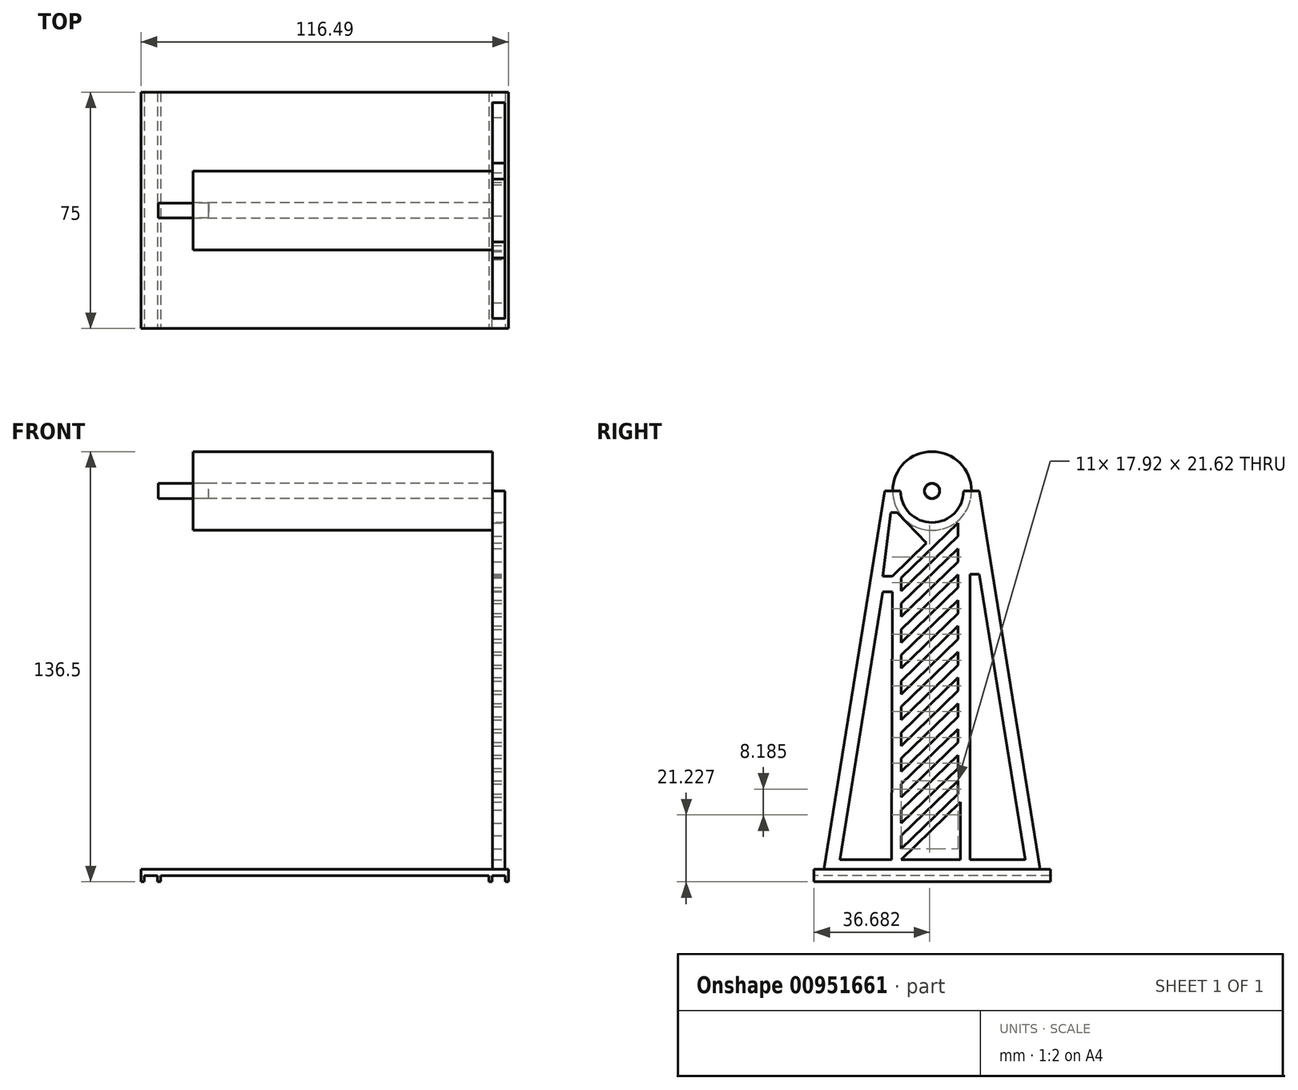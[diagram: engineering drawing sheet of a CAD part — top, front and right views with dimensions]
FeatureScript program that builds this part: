
annotation { "Feature Type Name" : "Feature", "Feature Type Description" : "" }
export const myFeature = defineFeature(function(context is Context, id is Id, definition is map)
    precondition{}
    {
        {
            var Q0;
            Q0=qCreatedBy(makeId("Right.planeOp"),FACE);
            var sketch = newSketch(context, id + "F0", { "sketchPlane" : qUnion([Q0])});
            skCircle(sketch, "E0", {"center": v(0, 0) * mm, "radius": 2.38 * mm});
            skSolve(sketch);
        }
        {
            var Q0;
            Q0=makeQuery(id+"F0.imprint","IMPRINT",FACE,{"disambiguationData":[TD([[makeQuery(id+"F0.imprint","IMPRINT",EDGE,{"derivedFrom":sQuery(id+"F0.wireOp",EDGE,"E0")}),1.0]])]});
            extrude(context, id + "F1", {"entities" : qUnion([Q0]), "depth" : 16 * mm, "offsetDistance" : 25 * mm});
        }
        {
            var Q0;
            Q0=makeQuery(id+"F1.opExtrude","CAP_FACE",FACE,{"disambiguationData":[OSD([sQuery(id+"F0.wireOp",EDGE,"E0")])],"isStart":false});
            var sketch = newSketch(context, id + "F2", { "sketchPlane" : qUnion([Q0])});
            skCircle(sketch, "E1.0.0", {"center": v(0, 0) * mm, "radius": 2.38 * mm});
            skCircle(sketch, "E2", {"center": v(0, 0) * mm, "radius": 12.5 * mm});
            skCircle(sketch, "E3", {"center": v(0, 0) * mm, "radius": 2.45 * mm});
            skSolve(sketch);
        }
        {
            var Q0;
            Q0 = qSketchRegion(id + "F2", true);
            extrude(context, id + "F3", {"entities" : qUnion([Q0]), "depth" : 90 * mm, "offsetDistance" : 25 * mm, "hasSecondDirection" : true, "secondDirectionOppositeDirection" : true, "secondDirectionDepth" : 5 * mm});
        }
        {
            var Q0;
            Q0=makeQuery(id+"F3.opExtrude","CAP_FACE",FACE,{"disambiguationData":[OSD([sQuery(id+"F2.wireOp",EDGE,"E2")])],"isStart":false});
            var sketch = newSketch(context, id + "F4", { "sketchPlane" : qUnion([Q0])});
            skCircle(sketch, "E4", {"center": v(0, 0) * mm, "radius": 10 * mm});
            skCircle(sketch, "E5", {"center": v(0, 0) * mm, "radius": 15 * mm});
            skLineSegment(sketch, "E6", {"start": v(0, 0) * mm, "end": v(15, 0) * mm});
            skLineSegment(sketch, "E7", {"start": v(0, 0) * mm, "end": v(-15, 0) * mm});
            skSolve(sketch);
        }
        {
            var Q0;
            {var subQ0=sQuery(id+"F4.wireOp",EDGE,"E6");var subQ1=sQuery(id+"F4.wireOp",EDGE,"E5");var subQ2=makeQuery(id+"F4.imprint","INTERSECT",VERTEX,{"derivedFrom":[subQ1,subQ0]});Q0=makeQuery(id+"F4.imprint","IMPRINT",FACE,{"disambiguationData":[TD([[makeQuery(id+"F4.imprint","IMPRINT",EDGE,{"disambiguationData":[TD([[subQ2,1.0]])],"derivedFrom":subQ1}),1.0]])]});}
            var Q1;
            {var subQ0=sQuery(id+"F4.wireOp",EDGE,"E6");var subQ1=sQuery(id+"F4.wireOp",EDGE,"E4");var subQ2=makeQuery(id+"F4.imprint","INTERSECT",VERTEX,{"derivedFrom":[subQ1,subQ0]});Q1=makeQuery(id+"F4.imprint","IMPRINT",FACE,{"disambiguationData":[TD([[makeQuery(id+"F4.imprint","IMPRINT",EDGE,{"disambiguationData":[TD([[subQ2,1.0]])],"derivedFrom":subQ1}),-1.0]])]});}
            extrude(context, id + "F5", {"entities" : qUnion([Q0, Q1]), "depth" : 4 * mm, "offsetDistance" : 25 * mm});
        }
        {
            var Q0;
            Q0=makeQuery(id+"F5.opExtrude","CAP_FACE",FACE,{"disambiguationData":[OSD([sQuery(id+"F4.wireOp",EDGE,"E4"),sQuery(id+"F4.wireOp",EDGE,"E5"),sQuery(id+"F4.wireOp",EDGE,"E6"),sQuery(id+"F4.wireOp",EDGE,"E7")])],"isStart":false});
            var sketch = newSketch(context, id + "F6", { "sketchPlane" : qUnion([Q0])});
            skArc(sketch, "E8.0.0", {"start": v(10, 0) * mm, "mid": v(0, -10) * mm, "end": v(-10, 0) * mm});
            skLineSegment(sketch, "E8.0.1", {"start": v(-10, 0) * mm, "end": v(-15, 0) * mm});
            skArc(sketch, "E8.0.2", {"start": v(-15, 0) * mm, "mid": v(0, -15) * mm, "end": v(15, 0) * mm});
            skLineSegment(sketch, "E8.0.3", {"start": v(15, 0) * mm, "end": v(10, 0) * mm});
            skLineSegment(sketch, "E9", {"start": v(-15, 0) * mm, "end": v(-34.26, -120) * mm});
            skLineSegment(sketch, "E10", {"start": v(15, 0) * mm, "end": v(34.26, -120) * mm});
            skLineSegment(sketch, "E11", {"start": v(34.26, -120) * mm, "end": v(-34.26, -120) * mm});
            skCircle(sketch, "E12.0.0", {"center": v(0, 0) * mm, "radius": 12.5 * mm});
            skLineSegment(sketch, "E13", {"start": v(0, 12.5) * mm, "end": v(18.93, 12.5) * mm});
            skSolve(sketch);
        }
        {
            var Q0;
            Q0=makeQuery(id+"F6.imprint","IMPRINT",FACE,{"disambiguationData":[TD([[makeQuery(id+"F6.imprint","IMPRINT",EDGE,{"derivedFrom":sQuery(id+"F6.wireOp",EDGE,"E8.0.2")}),-1.0]])]});
            var Q1;
            {var subQ0=sQuery(id+"F6.wireOp",EDGE,"E8.0.2");Q1=makeQuery(id+"F6.imprint","IMPRINT",FACE,{"disambiguationData":[TD([[makeQuery(id+"F6.imprint","IMPRINT",EDGE,{"derivedFrom":subQ0}),1.0]])]});}
            var Q2;
            {var subQ0=sQuery(id+"F6.wireOp",EDGE,"E8.0.0");Q2=makeQuery(id+"F6.imprint","IMPRINT",FACE,{"disambiguationData":[TD([[makeQuery(id+"F6.imprint","IMPRINT",EDGE,{"derivedFrom":subQ0}),-1.0]])]});}
            extrude(context, id + "F7", {"entities" : qUnion([Q0, Q1, Q2]), "operationType" : NewBodyOperationType.ADD, "oppositeDirection" : true, "depth" : 4 * mm, "offsetDistance" : 25 * mm});
        }
        {
            var Q0;
            Q0=makeQuery(id+"F7.boolean.opBoolean","MERGE",FACE,{"derivedFrom":[makeQuery(id+"F5.opExtrude","CAP_FACE",FACE,{"disambiguationData":[OSD([sQuery(id+"F4.wireOp",EDGE,"E4"),sQuery(id+"F4.wireOp",EDGE,"E5"),sQuery(id+"F4.wireOp",EDGE,"E6"),sQuery(id+"F4.wireOp",EDGE,"E7")])],"isStart":false}),makeQuery(id+"F7.opExtrude","CAP_FACE",FACE,{"disambiguationData":[OSD([sQuery(id+"F6.wireOp",EDGE,"E8.0.0"),sQuery(id+"F6.wireOp",EDGE,"E8.0.1"),sQuery(id+"F6.wireOp",EDGE,"E8.0.3"),sQuery(id+"F6.wireOp",EDGE,"E9"),sQuery(id+"F6.wireOp",EDGE,"E10"),sQuery(id+"F6.wireOp",EDGE,"E11")])],"isStart":true})]});
            var sketch = newSketch(context, id + "F8", { "sketchPlane" : qUnion([Q0])});
            skLineSegment(sketch, "E14", {"start": v(-9.74, -27.54) * mm, "end": v(8.18, -10.11) * mm});
            skLineSegment(sketch, "E15", {"start": v(8.18, -10.11) * mm, "end": v(8.18, -14.3) * mm});
            skLineSegment(sketch, "E16", {"start": v(8.18, -14.3) * mm, "end": v(-9.74, -31.73) * mm});
            skLineSegment(sketch, "E17", {"start": v(-9.74, -31.73) * mm, "end": v(-9.74, -27.54) * mm});
            skLineSegment(sketch, "E18", {"start": v(-9.74, -35.73) * mm, "end": v(8.18, -18.3) * mm});
            skLineSegment(sketch, "E19", {"start": v(8.18, -18.3) * mm, "end": v(8.18, -22.48) * mm});
            skLineSegment(sketch, "E20", {"start": v(8.18, -22.48) * mm, "end": v(-9.74, -39.91) * mm});
            skLineSegment(sketch, "E21", {"start": v(-9.74, -39.91) * mm, "end": v(-9.74, -35.73) * mm});
            skLineSegment(sketch, "E22", {"start": v(-9.74, -43.91) * mm, "end": v(8.18, -26.48) * mm});
            skLineSegment(sketch, "E23", {"start": v(8.18, -26.48) * mm, "end": v(8.18, -30.67) * mm});
            skLineSegment(sketch, "E24", {"start": v(8.18, -30.67) * mm, "end": v(-9.74, -48.1) * mm});
            skLineSegment(sketch, "E25", {"start": v(-9.74, -48.1) * mm, "end": v(-9.74, -43.91) * mm});
            skLineSegment(sketch, "E26", {"start": v(-9.74, -52.1) * mm, "end": v(8.18, -34.67) * mm});
            skLineSegment(sketch, "E27", {"start": v(8.18, -34.67) * mm, "end": v(8.18, -38.85) * mm});
            skLineSegment(sketch, "E28", {"start": v(8.18, -38.85) * mm, "end": v(-9.74, -56.28) * mm});
            skLineSegment(sketch, "E29", {"start": v(-9.74, -56.28) * mm, "end": v(-9.74, -52.1) * mm});
            skLineSegment(sketch, "E30", {"start": v(-9.74, -60.28) * mm, "end": v(8.18, -42.85) * mm});
            skLineSegment(sketch, "E31", {"start": v(8.18, -42.85) * mm, "end": v(8.18, -47.04) * mm});
            skLineSegment(sketch, "E32", {"start": v(8.18, -47.04) * mm, "end": v(-9.74, -64.47) * mm});
            skLineSegment(sketch, "E33", {"start": v(-9.74, -64.47) * mm, "end": v(-9.74, -60.28) * mm});
            skLineSegment(sketch, "E34", {"start": v(-9.74, -68.47) * mm, "end": v(8.18, -51.04) * mm});
            skLineSegment(sketch, "E35", {"start": v(8.18, -51.04) * mm, "end": v(8.18, -55.22) * mm});
            skLineSegment(sketch, "E36", {"start": v(8.18, -55.22) * mm, "end": v(-9.74, -72.66) * mm});
            skLineSegment(sketch, "E37", {"start": v(-9.74, -72.66) * mm, "end": v(-9.74, -68.47) * mm});
            skLineSegment(sketch, "E38", {"start": v(-9.74, -76.66) * mm, "end": v(8.18, -59.22) * mm});
            skLineSegment(sketch, "E39", {"start": v(8.18, -59.22) * mm, "end": v(8.18, -63.4) * mm});
            skLineSegment(sketch, "E40", {"start": v(8.18, -63.4) * mm, "end": v(-9.74, -80.84) * mm});
            skLineSegment(sketch, "E41", {"start": v(-9.74, -80.84) * mm, "end": v(-9.74, -76.66) * mm});
            skLineSegment(sketch, "E42", {"start": v(-9.74, -84.84) * mm, "end": v(8.18, -67.4) * mm});
            skLineSegment(sketch, "E43", {"start": v(8.18, -67.4) * mm, "end": v(8.18, -71.6) * mm});
            skLineSegment(sketch, "E44", {"start": v(8.18, -71.6) * mm, "end": v(-9.74, -89.03) * mm});
            skLineSegment(sketch, "E45", {"start": v(-9.74, -89.03) * mm, "end": v(-9.74, -84.84) * mm});
            skLineSegment(sketch, "E46", {"start": v(-9.74, -93.03) * mm, "end": v(8.18, -75.6) * mm});
            skLineSegment(sketch, "E47", {"start": v(8.18, -75.6) * mm, "end": v(8.18, -79.78) * mm});
            skLineSegment(sketch, "E48", {"start": v(8.18, -79.78) * mm, "end": v(-9.74, -97.21) * mm});
            skLineSegment(sketch, "E49", {"start": v(-9.74, -97.21) * mm, "end": v(-9.74, -93.03) * mm});
            skLineSegment(sketch, "E50", {"start": v(-9.74, -101.21) * mm, "end": v(8.18, -83.78) * mm});
            skLineSegment(sketch, "E51", {"start": v(8.18, -83.78) * mm, "end": v(8.18, -87.96) * mm});
            skLineSegment(sketch, "E52", {"start": v(8.18, -87.96) * mm, "end": v(-9.74, -105.4) * mm});
            skLineSegment(sketch, "E53", {"start": v(-9.74, -105.4) * mm, "end": v(-9.74, -101.21) * mm});
            skLineSegment(sketch, "E54", {"start": v(-9.74, -109.4) * mm, "end": v(8.18, -91.96) * mm});
            skLineSegment(sketch, "E55", {"start": v(8.18, -91.96) * mm, "end": v(8.18, -96.15) * mm});
            skLineSegment(sketch, "E56", {"start": v(8.18, -96.15) * mm, "end": v(-9.74, -113.58) * mm});
            skLineSegment(sketch, "E57", {"start": v(-9.74, -113.58) * mm, "end": v(-9.74, -109.4) * mm});
            skLineSegment(sketch, "E58", {"start": v(-9.74, -116.96) * mm, "end": v(9, -98.73) * mm});
            skLineSegment(sketch, "E59", {"start": v(9, -98.73) * mm, "end": v(12, -98.73) * mm});
            skLineSegment(sketch, "E60", {"start": v(12, -98.73) * mm, "end": v(12, -26.38) * mm});
            skLineSegment(sketch, "E61", {"start": v(12, -26.38) * mm, "end": v(15, -26.38) * mm});
            skLineSegment(sketch, "E62", {"start": v(15, -26.38) * mm, "end": v(29.54, -116.96) * mm});
            skLineSegment(sketch, "E63", {"start": v(29.54, -116.96) * mm, "end": v(-9.74, -116.96) * mm});
            skLineSegment(sketch, "E64", {"start": v(-12.83, -116.96) * mm, "end": v(-29.24, -116.96) * mm});
            skLineSegment(sketch, "E65", {"start": v(-29.24, -116.96) * mm, "end": v(-15.6, -31.99) * mm});
            skLineSegment(sketch, "E66", {"start": v(-15.6, -31.99) * mm, "end": v(-12.6, -31.99) * mm});
            skLineSegment(sketch, "E67", {"start": v(-12.6, -31.99) * mm, "end": v(-12.83, -116.96) * mm});
            skLineSegment(sketch, "E68", {"start": v(-15.6, -27.04) * mm, "end": v(-12.6, -27.04) * mm});
            skLineSegment(sketch, "E69", {"start": v(-12.6, -27.04) * mm, "end": v(-1.72, -16.46) * mm});
            skLineSegment(sketch, "E70", {"start": v(-1.72, -16.46) * mm, "end": v(-11.07, -6.84) * mm});
            skLineSegment(sketch, "E71", {"start": v(-11.07, -6.84) * mm, "end": v(-13.07, -6.84) * mm});
            skLineSegment(sketch, "E72", {"start": v(-13.07, -6.84) * mm, "end": v(-15.6, -27.04) * mm});
            skLineSegment(sketch, "E73", {"start": v(9, -98.73) * mm, "end": v(9, -116.96) * mm});
            skLineSegment(sketch, "E74", {"start": v(12, -98.73) * mm, "end": v(12, -116.96) * mm});
            skSolve(sketch);
        }
        {
            var Q0;
            Q0=makeQuery(id+"F8.imprint","IMPRINT",FACE,{"disambiguationData":[TD([[makeQuery(id+"F8.imprint","IMPRINT",EDGE,{"derivedFrom":sQuery(id+"F8.wireOp",EDGE,"E14")}),-1.0]])]});
            var Q1;
            Q1=makeQuery(id+"F8.imprint","IMPRINT",FACE,{"disambiguationData":[TD([[makeQuery(id+"F8.imprint","IMPRINT",EDGE,{"derivedFrom":sQuery(id+"F8.wireOp",EDGE,"E18")}),-1.0]])]});
            var Q2;
            Q2=makeQuery(id+"F8.imprint","IMPRINT",FACE,{"disambiguationData":[TD([[makeQuery(id+"F8.imprint","IMPRINT",EDGE,{"derivedFrom":sQuery(id+"F8.wireOp",EDGE,"E22")}),-1.0]])]});
            var Q3;
            Q3=makeQuery(id+"F8.imprint","IMPRINT",FACE,{"disambiguationData":[TD([[makeQuery(id+"F8.imprint","IMPRINT",EDGE,{"derivedFrom":sQuery(id+"F8.wireOp",EDGE,"E26")}),-1.0]])]});
            var Q4;
            Q4=makeQuery(id+"F8.imprint","IMPRINT",FACE,{"disambiguationData":[TD([[makeQuery(id+"F8.imprint","IMPRINT",EDGE,{"derivedFrom":sQuery(id+"F8.wireOp",EDGE,"E30")}),-1.0]])]});
            var Q5;
            Q5=makeQuery(id+"F8.imprint","IMPRINT",FACE,{"disambiguationData":[TD([[makeQuery(id+"F8.imprint","IMPRINT",EDGE,{"derivedFrom":sQuery(id+"F8.wireOp",EDGE,"E34")}),-1.0]])]});
            var Q6;
            Q6=makeQuery(id+"F8.imprint","IMPRINT",FACE,{"disambiguationData":[TD([[makeQuery(id+"F8.imprint","IMPRINT",EDGE,{"derivedFrom":sQuery(id+"F8.wireOp",EDGE,"E38")}),-1.0]])]});
            var Q7;
            Q7=makeQuery(id+"F8.imprint","IMPRINT",FACE,{"disambiguationData":[TD([[makeQuery(id+"F8.imprint","IMPRINT",EDGE,{"derivedFrom":sQuery(id+"F8.wireOp",EDGE,"E42")}),-1.0]])]});
            var Q8;
            Q8=makeQuery(id+"F8.imprint","IMPRINT",FACE,{"disambiguationData":[TD([[makeQuery(id+"F8.imprint","IMPRINT",EDGE,{"derivedFrom":sQuery(id+"F8.wireOp",EDGE,"E46")}),-1.0]])]});
            var Q9;
            Q9=makeQuery(id+"F8.imprint","IMPRINT",FACE,{"disambiguationData":[TD([[makeQuery(id+"F8.imprint","IMPRINT",EDGE,{"derivedFrom":sQuery(id+"F8.wireOp",EDGE,"E50")}),-1.0]])]});
            var Q10;
            Q10=makeQuery(id+"F8.imprint","IMPRINT",FACE,{"disambiguationData":[TD([[makeQuery(id+"F8.imprint","IMPRINT",EDGE,{"derivedFrom":sQuery(id+"F8.wireOp",EDGE,"E54")}),-1.0]])]});
            var Q11;
            Q11=makeQuery(id+"F8.imprint","IMPRINT",FACE,{"disambiguationData":[TD([[makeQuery(id+"F8.imprint","IMPRINT",EDGE,{"derivedFrom":sQuery(id+"F8.wireOp",EDGE,"E68")}),1.0]])]});
            var Q12;
            Q12=makeQuery(id+"F8.imprint","IMPRINT",FACE,{"disambiguationData":[TD([[makeQuery(id+"F8.imprint","IMPRINT",EDGE,{"derivedFrom":sQuery(id+"F8.wireOp",EDGE,"E64")}),-1.0]])]});
            var Q13;
            Q13=makeQuery(id+"F8.imprint","IMPRINT",FACE,{"disambiguationData":[TD([[makeQuery(id+"F8.imprint","IMPRINT",EDGE,{"derivedFrom":sQuery(id+"F8.wireOp",EDGE,"E60")}),-1.0]])]});
            var Q14;
            {var subQ0=sQuery(id+"F8.wireOp",EDGE,"E58");Q14=makeQuery(id+"F8.imprint","IMPRINT",FACE,{"disambiguationData":[TD([[makeQuery(id+"F8.imprint","IMPRINT",EDGE,{"derivedFrom":subQ0}),-1.0]])]});}
            extrude(context, id + "F9", {"entities" : qUnion([Q0, Q1, Q2, Q3, Q4, Q5, Q6, Q7, Q8, Q9, Q10, Q11, Q12, Q13, Q14]), "operationType" : NewBodyOperationType.REMOVE, "oppositeDirection" : true, "depth" : 25 * mm, "offsetDistance" : 25 * mm});
        }
        {
            var Q0;
            Q0=makeQuery(id+"F7.opExtrude","SWEPT_FACE",FACE,{"disambiguationData":[OSD([sQuery(id+"F6.wireOp",EDGE,"E11")])]});
            var sketch = newSketch(context, id + "F10", { "sketchPlane" : qUnion([Q0])});
            skLineSegment(sketch, "E75.0.0", {"start": v(110, -34.26) * mm, "end": v(110, 34.26) * mm});
            skLineSegment(sketch, "E75.0.1", {"start": v(110, 34.26) * mm, "end": v(106, 34.26) * mm});
            skLineSegment(sketch, "E75.0.2", {"start": v(106, 34.26) * mm, "end": v(106, -34.26) * mm});
            skLineSegment(sketch, "E75.0.3", {"start": v(106, -34.26) * mm, "end": v(110, -34.26) * mm});
            skLineSegment(sketch, "E76", {"start": v(111.08, 37.46) * mm, "end": v(111.08, -37.54) * mm});
            skLineSegment(sketch, "E77", {"start": v(111.08, -37.54) * mm, "end": v(-5.42, -37.54) * mm});
            skLineSegment(sketch, "E78", {"start": v(-5.42, -37.54) * mm, "end": v(-5.43, 37.46) * mm});
            skLineSegment(sketch, "E79", {"start": v(-5.43, 37.46) * mm, "end": v(111.08, 37.46) * mm});
            skLineSegment(sketch, "E80", {"start": v(110.08, 37.46) * mm, "end": v(110.08, -37.54) * mm});
            skLineSegment(sketch, "E81", {"start": v(105.92, -37.54) * mm, "end": v(105.92, 37.46) * mm});
            skLineSegment(sketch, "E82", {"start": v(-4.43, 37.46) * mm, "end": v(-4.42, -37.54) * mm});
            skLineSegment(sketch, "E83", {"start": v(-0.28, 37.46) * mm, "end": v(-0.27, -37.54) * mm});
            skLineSegment(sketch, "E84", {"start": v(0.72, 37.46) * mm, "end": v(0.73, -37.54) * mm});
            skLineSegment(sketch, "E85", {"start": v(104.92, 37.46) * mm, "end": v(104.93, -37.54) * mm});
            skSolve(sketch);
        }
        {
            var Q0;
            {var subQ0=sQuery(id+"F10.wireOp",EDGE,"E84");Q0=makeQuery(id+"F10.imprint","IMPRINT",FACE,{"disambiguationData":[TD([[makeQuery(id+"F10.imprint","IMPRINT",EDGE,{"derivedFrom":subQ0}),1.0]])]});}
            var Q1;
            {var subQ0=sQuery(id+"F10.wireOp",EDGE,"E82");Q1=makeQuery(id+"F10.imprint","IMPRINT",FACE,{"disambiguationData":[TD([[makeQuery(id+"F10.imprint","IMPRINT",EDGE,{"derivedFrom":subQ0}),1.0]])]});}
            var Q2;
            {var subQ0=sQuery(id+"F10.wireOp",EDGE,"E78");Q2=makeQuery(id+"F10.imprint","IMPRINT",FACE,{"disambiguationData":[TD([[makeQuery(id+"F10.imprint","IMPRINT",EDGE,{"derivedFrom":subQ0}),-1.0]])]});}
            var Q3;
            {var subQ0=sQuery(id+"F10.wireOp",EDGE,"E83");Q3=makeQuery(id+"F10.imprint","IMPRINT",FACE,{"disambiguationData":[TD([[makeQuery(id+"F10.imprint","IMPRINT",EDGE,{"derivedFrom":subQ0}),1.0]])]});}
            var Q4;
            {var subQ0=sQuery(id+"F10.wireOp",EDGE,"E76");Q4=makeQuery(id+"F10.imprint","IMPRINT",FACE,{"disambiguationData":[TD([[makeQuery(id+"F10.imprint","IMPRINT",EDGE,{"derivedFrom":subQ0}),-1.0]])]});}
            var Q5;
            {var subQ0=sQuery(id+"F10.wireOp",EDGE,"E81");Q5=makeQuery(id+"F10.imprint","IMPRINT",FACE,{"disambiguationData":[TD([[makeQuery(id+"F10.imprint","IMPRINT",EDGE,{"derivedFrom":subQ0}),1.0]])]});}
            var Q6;
            Q6=makeQuery(id+"F10.imprint","IMPRINT",FACE,{"disambiguationData":[TD([[makeQuery(id+"F10.imprint","IMPRINT",EDGE,{"derivedFrom":sQuery(id+"F10.wireOp",EDGE,"E75.0.0")}),-1.0]])]});
            var Q7;
            Q7=makeQuery(id+"F10.imprint","IMPRINT",FACE,{"disambiguationData":[TD([[makeQuery(id+"F10.imprint","IMPRINT",EDGE,{"derivedFrom":sQuery(id+"F10.wireOp",EDGE,"E75.0.0")}),1.0]])]});
            extrude(context, id + "F11", {"entities" : qUnion([Q0, Q1, Q2, Q3, Q4, Q5, Q6, Q7]), "depth" : 2 * mm, "offsetDistance" : 25 * mm});
        }
        {
            var Q0;
            {var subQ0=sQuery(id+"F10.wireOp",EDGE,"E76");Q0=makeQuery(id+"F10.imprint","IMPRINT",FACE,{"disambiguationData":[TD([[makeQuery(id+"F10.imprint","IMPRINT",EDGE,{"derivedFrom":subQ0}),-1.0]])]});}
            var Q1;
            {var subQ0=sQuery(id+"F10.wireOp",EDGE,"E81");Q1=makeQuery(id+"F10.imprint","IMPRINT",FACE,{"disambiguationData":[TD([[makeQuery(id+"F10.imprint","IMPRINT",EDGE,{"derivedFrom":subQ0}),1.0]])]});}
            var Q2;
            {var subQ0=sQuery(id+"F10.wireOp",EDGE,"E78");Q2=makeQuery(id+"F10.imprint","IMPRINT",FACE,{"disambiguationData":[TD([[makeQuery(id+"F10.imprint","IMPRINT",EDGE,{"derivedFrom":subQ0}),-1.0]])]});}
            var Q3;
            {var subQ0=sQuery(id+"F10.wireOp",EDGE,"E83");Q3=makeQuery(id+"F10.imprint","IMPRINT",FACE,{"disambiguationData":[TD([[makeQuery(id+"F10.imprint","IMPRINT",EDGE,{"derivedFrom":subQ0}),1.0]])]});}
            extrude(context, id + "F12", {"entities" : qUnion([Q0, Q1, Q2, Q3]), "operationType" : NewBodyOperationType.ADD, "depth" : 4 * mm, "offsetDistance" : 25 * mm});
        }
    });
